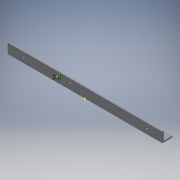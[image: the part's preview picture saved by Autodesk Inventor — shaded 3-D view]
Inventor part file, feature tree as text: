
AUTODESK INVENTOR PART (.ipt)
format: ipt  version: 2018 (Build 220112000, 112)  size: 141,312 bytes
history: native  units: mm
features: sketch x7, extrude x6, reference x4, other x4, projected_geometry x2
ambient origin geometry x8: Origin, YZ Plane, XZ Plane, XY Plane, X Axis, Y Axis, Z Axis, Center Point
bodies: Solid1 (feature_tree)
feature tree (23):
  extrude  "Extrusion1"  Depth=15.08mm
  extrude  "Extrusion2"  Depth=2.05mm
  extrude  "Extrusion3"  Depth=13.03mm
  sketch  "Sketch4"  dims[d8=93.5mm d9=8.0mm]
  extrude  "Extrusion6"  Depth=8.0mm
  extrude  "Extrusion7"  Depth=2.05mm TaperAngle=0.0deg
  extrude  "Extrusion8"  Depth=3.2mm
  sketch  "Sketch1"  dims[d0=234.5mm d1=15.08mm]
  sketch  "Sketch2"  dims[d2=2.05mm d3=0.0mm d4=2.05mm]
  sketch  "Sketch3"  dims[d5=13.03mm d6=0.0mm d7=93.5mm]
  sketch  "Sketch6"  dims[d10=8.0mm d11=2.05mm d12=0.0mm]
  reference  "Reference1"
  sketch  "Sketch7"  dims[d13=3.2mm d14=3.2mm]
  projected_geometry  "Projected Loop1"
  reference  "Reference2"
  sketch  "Sketch8"  dims[d15=3.8mm d26=3.0mm d27=0.0mm d28=10.0mm d29=0.0mm d30=10.0mm d31=0.0mm]
  projected_geometry  "Projected Loop2"
  reference  "Reference3"
  reference  "Reference4"
  other  "<userpath>\Documents\optoelectronics\CAD\Bigdriver_box\Big_housing.iam"
  other  "Big_housing.iam"
  other  "source:1"
  other  "Large_frontplatte:1"
